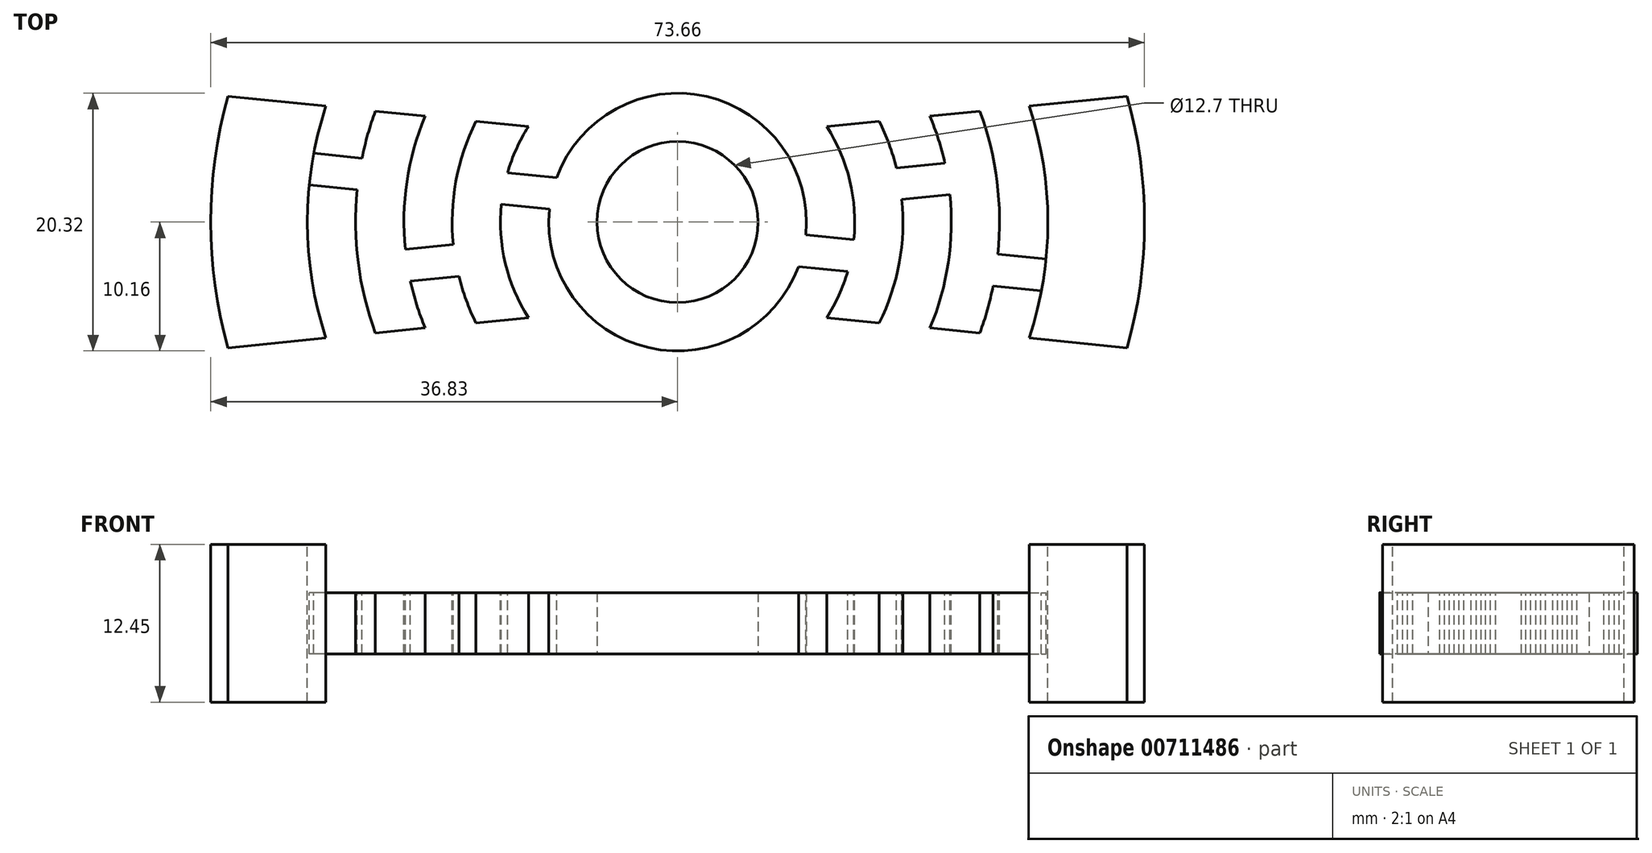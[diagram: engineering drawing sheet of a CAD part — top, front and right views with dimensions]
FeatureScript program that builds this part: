
annotation { "Feature Type Name" : "Feature", "Feature Type Description" : "" }
export const myFeature = defineFeature(function(context is Context, id is Id, definition is map)
    precondition{}
    {
        {
            var Q0;
            Q0=qCreatedBy(makeId("Top.planeOp"),FACE);
            var sketch = newSketch(context, id + "F0", { "sketchPlane" : qUnion([Q0])});
            skCircle(sketch, "E0", {"center": v(0, 0) * mm, "radius": 6.35 * mm});
            skCircle(sketch, "E1", {"center": v(0, 0) * mm, "radius": 10.16 * mm});
            skLineSegment(sketch, "E2", {"start": v(0, 6.35) * mm, "end": v(-37.9, 10.16) * mm});
            skLineSegment(sketch, "E3", {"start": v(0, -6.35) * mm, "end": v(-37.9, -10.16) * mm});
            skLineSegment(sketch, "E4", {"start": v(0, 6.35) * mm, "end": v(37.9, 10.16) * mm});
            skLineSegment(sketch, "E5", {"start": v(0, -6.35) * mm, "end": v(37.9, -10.16) * mm});
            skLineSegment(sketch, "E6", {"start": v(0, 0) * mm, "end": v(40.64, 0) * mm});
            skLineSegment(sketch, "E7", {"start": v(0, 0) * mm, "end": v(-40.64, 0) * mm});
            skCircle(sketch, "E8", {"center": v(0, 0) * mm, "radius": 39.25 * mm});
            skSolve(sketch);
        }
        {
            var Q0;
            {var subQ0=sQuery(id+"F0.wireOp",EDGE,"E4");var subQ1=sQuery(id+"F0.wireOp",EDGE,"E1");var subQ2=makeQuery(id+"F0.imprint","INTERSECT",VERTEX,{"derivedFrom":[subQ1,subQ0]});Q0=makeQuery(id+"F0.imprint","IMPRINT",FACE,{"disambiguationData":[TD([[makeQuery(id+"F0.imprint","IMPRINT",EDGE,{"disambiguationData":[TD([[subQ2,1.0]])],"derivedFrom":subQ1}),-1.0]])]});}
            var Q1;
            {var subQ0=sQuery(id+"F0.wireOp",EDGE,"E2");var subQ1=sQuery(id+"F0.wireOp",EDGE,"E1");var subQ2=makeQuery(id+"F0.imprint","INTERSECT",VERTEX,{"derivedFrom":[subQ1,subQ0]});Q1=makeQuery(id+"F0.imprint","IMPRINT",FACE,{"disambiguationData":[TD([[makeQuery(id+"F0.imprint","IMPRINT",EDGE,{"disambiguationData":[TD([[subQ2,-1.0]])],"derivedFrom":subQ1}),-1.0]])]});}
            var Q2;
            {var subQ0=sQuery(id+"F0.wireOp",EDGE,"E7");var subQ1=sQuery(id+"F0.wireOp",EDGE,"E1");var subQ2=makeQuery(id+"F0.imprint","INTERSECT",VERTEX,{"derivedFrom":[subQ1,subQ0]});Q2=makeQuery(id+"F0.imprint","IMPRINT",FACE,{"disambiguationData":[TD([[makeQuery(id+"F0.imprint","IMPRINT",EDGE,{"disambiguationData":[TD([[subQ2,-1.0]])],"derivedFrom":subQ1}),-1.0]])]});}
            var Q3;
            {var subQ0=sQuery(id+"F0.wireOp",EDGE,"E6");var subQ1=sQuery(id+"F0.wireOp",EDGE,"E1");var subQ2=makeQuery(id+"F0.imprint","INTERSECT",VERTEX,{"derivedFrom":[subQ1,subQ0]});Q3=makeQuery(id+"F0.imprint","IMPRINT",FACE,{"disambiguationData":[TD([[makeQuery(id+"F0.imprint","IMPRINT",EDGE,{"disambiguationData":[TD([[subQ2,1.0]])],"derivedFrom":subQ1}),-1.0]])]});}
            var Q4;
            {var subQ0=sQuery(id+"F0.wireOp",EDGE,"E2");var subQ5=sQuery(id+"F0.wireOp",EDGE,"E1");var subQ6=makeQuery(id+"F0.imprint","INTERSECT",VERTEX,{"derivedFrom":[subQ5,subQ0]});Q4=makeQuery(id+"F0.imprint","IMPRINT",FACE,{"disambiguationData":[TD([[makeQuery(id+"F0.imprint","IMPRINT",EDGE,{"disambiguationData":[TD([[subQ6,-1.0]])],"derivedFrom":subQ5}),1.0]])]});}
            var Q5;
            {var subQ3=sQuery(id+"F0.wireOp",EDGE,"E7");var subQ5=sQuery(id+"F0.wireOp",EDGE,"E1");var subQ6=makeQuery(id+"F0.imprint","INTERSECT",VERTEX,{"derivedFrom":[subQ5,subQ3]});Q5=makeQuery(id+"F0.imprint","IMPRINT",FACE,{"disambiguationData":[TD([[makeQuery(id+"F0.imprint","IMPRINT",EDGE,{"disambiguationData":[TD([[subQ6,-1.0]])],"derivedFrom":subQ5}),1.0]])]});}
            var Q6;
            {var subQ3=sQuery(id+"F0.wireOp",EDGE,"E6");var subQ5=sQuery(id+"F0.wireOp",EDGE,"E1");var subQ6=makeQuery(id+"F0.imprint","INTERSECT",VERTEX,{"derivedFrom":[subQ5,subQ3]});Q6=makeQuery(id+"F0.imprint","IMPRINT",FACE,{"disambiguationData":[TD([[makeQuery(id+"F0.imprint","IMPRINT",EDGE,{"disambiguationData":[TD([[subQ6,1.0]])],"derivedFrom":subQ5}),1.0]])]});}
            var Q7;
            {var subQ0=sQuery(id+"F0.wireOp",EDGE,"E4");var subQ5=sQuery(id+"F0.wireOp",EDGE,"E1");var subQ6=makeQuery(id+"F0.imprint","INTERSECT",VERTEX,{"derivedFrom":[subQ5,subQ0]});Q7=makeQuery(id+"F0.imprint","IMPRINT",FACE,{"disambiguationData":[TD([[makeQuery(id+"F0.imprint","IMPRINT",EDGE,{"disambiguationData":[TD([[subQ6,1.0]])],"derivedFrom":subQ5}),1.0]])]});}
            var Q8;
            {var subQ0=sQuery(id+"F0.wireOp",EDGE,"E4");var subQ1=sQuery(id+"F0.wireOp",EDGE,"E1");var subQ2=makeQuery(id+"F0.imprint","INTERSECT",VERTEX,{"derivedFrom":[subQ1,subQ0]});Q8=makeQuery(id+"F0.imprint","IMPRINT",FACE,{"disambiguationData":[TD([[makeQuery(id+"F0.imprint","IMPRINT",EDGE,{"disambiguationData":[TD([[subQ2,-1.0]])],"derivedFrom":subQ1}),1.0]])]});}
            var Q9;
            {var subQ0=sQuery(id+"F0.wireOp",EDGE,"E3");var subQ1=sQuery(id+"F0.wireOp",EDGE,"E1");var subQ2=makeQuery(id+"F0.imprint","INTERSECT",VERTEX,{"derivedFrom":[subQ1,subQ0]});Q9=makeQuery(id+"F0.imprint","IMPRINT",FACE,{"disambiguationData":[TD([[makeQuery(id+"F0.imprint","IMPRINT",EDGE,{"disambiguationData":[TD([[subQ2,-1.0]])],"derivedFrom":subQ1}),1.0]])]});}
            extrude(context, id + "F1", {"entities" : qUnion([Q0, Q1, Q2, Q3, Q4, Q5, Q6, Q7, Q8, Q9]), "depth" : 4.83 * mm, "offsetDistance" : 25.4 * mm});
        }
        {
            var Q0;
            Q0=makeQuery(id+"F1.opExtrude","CAP_FACE",FACE,{"disambiguationData":[OSD([sQuery(id+"F0.wireOp",EDGE,"E0"),sQuery(id+"F0.wireOp",EDGE,"E1"),sQuery(id+"F0.wireOp",EDGE,"E2"),sQuery(id+"F0.wireOp",EDGE,"E3"),sQuery(id+"F0.wireOp",EDGE,"E4"),sQuery(id+"F0.wireOp",EDGE,"E5"),sQuery(id+"F0.wireOp",EDGE,"liuHo2mv-Kwf8-5aol-AB9t-589r57ZSycez"),sQuery(id+"F0.wireOp",EDGE,"nakFOlJR-s7SA-ednX-MnhK-JYGa1BLhNWg9")])],"isStart":false});
            var sketch = newSketch(context, id + "F2", { "sketchPlane" : qUnion([Q0])});
            skCircle(sketch, "E9", {"center": v(0, 0) * mm, "radius": 6.35 * mm});
            skCircle(sketch, "E10", {"center": v(0, 0) * mm, "radius": 10.16 * mm});
            skCircle(sketch, "E11", {"center": v(0, 0) * mm, "radius": 39.25 * mm});
            skCircle(sketch, "E12", {"center": v(0, 0) * mm, "radius": 33.02 * mm});
            skCircle(sketch, "E13", {"center": v(0, 0) * mm, "radius": 25.4 * mm});
            skCircle(sketch, "E14", {"center": v(0, 0) * mm, "radius": 21.59 * mm});
            skCircle(sketch, "E15", {"center": v(0, 0) * mm, "radius": 29.21 * mm});
            skCircle(sketch, "E16", {"center": v(0, 0) * mm, "radius": 13.97 * mm});
            skCircle(sketch, "E17", {"center": v(0, 0) * mm, "radius": 17.78 * mm});
            skCircle(sketch, "E18", {"center": v(0, 0) * mm, "radius": 2.54 * mm});
            skLineSegment(sketch, "E19", {"start": v(0, -2.54) * mm, "end": v(-38.72, -6.43) * mm});
            skLineSegment(sketch, "E20", {"start": v(0, 2.54) * mm, "end": v(-38.72, 6.43) * mm});
            skLineSegment(sketch, "E21", {"start": v(0, -2.54) * mm, "end": v(38.72, -6.43) * mm});
            skLineSegment(sketch, "E22", {"start": v(0, 2.54) * mm, "end": v(38.72, 6.43) * mm});
            skLineSegment(sketch, "E23", {"start": v(0, 0) * mm, "end": v(-39.05, 3.92) * mm});
            skLineSegment(sketch, "E24", {"start": v(0, 0) * mm, "end": v(39.05, 3.92) * mm});
            skLineSegment(sketch, "E25", {"start": v(0, 0) * mm, "end": v(39.05, -3.92) * mm});
            skLineSegment(sketch, "E26", {"start": v(0, 0) * mm, "end": v(-39.05, -3.92) * mm});
            skCircle(sketch, "E27", {"center": v(0, 0) * mm, "radius": 36.83 * mm});
            skCircle(sketch, "E28", {"center": v(0.53, -0.92) * mm, "radius": 41.7 * mm});
            skSolve(sketch);
        }
        {
            var Q0;
            {var subQ0=sQuery(id+"F2.wireOp",EDGE,"E20");var subQ1=sQuery(id+"F2.wireOp",EDGE,"E14");var subQ2=makeQuery(id+"F2.imprint","INTERSECT",VERTEX,{"derivedFrom":[subQ1,subQ0]});Q0=makeQuery(id+"F2.imprint","IMPRINT",FACE,{"disambiguationData":[TD([[makeQuery(id+"F2.imprint","IMPRINT",EDGE,{"disambiguationData":[TD([[subQ2,1.0]])],"derivedFrom":subQ1}),1.0]])]});}
            var Q1;
            {var subQ0=sQuery(id+"F2.wireOp",EDGE,"E20");var subQ1=sQuery(id+"F2.wireOp",EDGE,"E14");var subQ2=makeQuery(id+"F2.imprint","INTERSECT",VERTEX,{"derivedFrom":[subQ1,subQ0]});Q1=makeQuery(id+"F2.imprint","IMPRINT",FACE,{"disambiguationData":[TD([[makeQuery(id+"F2.imprint","IMPRINT",EDGE,{"disambiguationData":[TD([[subQ2,-1.0]])],"derivedFrom":subQ1}),1.0]])]});}
            var Q2;
            {var subQ0=sQuery(id+"F2.wireOp",EDGE,"E21");var subQ1=sQuery(id+"F2.wireOp",EDGE,"E14");var subQ2=makeQuery(id+"F2.imprint","INTERSECT",VERTEX,{"derivedFrom":[subQ1,subQ0]});Q2=makeQuery(id+"F2.imprint","IMPRINT",FACE,{"disambiguationData":[TD([[makeQuery(id+"F2.imprint","IMPRINT",EDGE,{"disambiguationData":[TD([[subQ2,1.0]])],"derivedFrom":subQ1}),1.0]])]});}
            var Q3;
            {var subQ0=sQuery(id+"F2.wireOp",EDGE,"E19");var subQ1=sQuery(id+"F2.wireOp",EDGE,"E14");var subQ2=makeQuery(id+"F2.imprint","INTERSECT",VERTEX,{"derivedFrom":[subQ1,subQ0]});Q3=makeQuery(id+"F2.imprint","IMPRINT",FACE,{"disambiguationData":[TD([[makeQuery(id+"F2.imprint","IMPRINT",EDGE,{"disambiguationData":[TD([[subQ2,-1.0]])],"derivedFrom":subQ1}),1.0]])]});}
            var Q4;
            {var subQ0=sQuery(id+"F2.wireOp",EDGE,"E19");var subQ1=sQuery(id+"F2.wireOp",EDGE,"E13");var subQ2=makeQuery(id+"F2.imprint","INTERSECT",VERTEX,{"derivedFrom":[subQ1,subQ0]});Q4=makeQuery(id+"F2.imprint","IMPRINT",FACE,{"disambiguationData":[TD([[makeQuery(id+"F2.imprint","IMPRINT",EDGE,{"disambiguationData":[TD([[subQ2,-1.0]])],"derivedFrom":subQ1}),-1.0]])]});}
            var Q5;
            {var subQ0=sQuery(id+"F2.wireOp",EDGE,"E23");var subQ1=sQuery(id+"F2.wireOp",EDGE,"E13");var subQ2=makeQuery(id+"F2.imprint","INTERSECT",VERTEX,{"derivedFrom":[subQ1,subQ0]});Q5=makeQuery(id+"F2.imprint","IMPRINT",FACE,{"disambiguationData":[TD([[makeQuery(id+"F2.imprint","IMPRINT",EDGE,{"disambiguationData":[TD([[subQ2,-1.0]])],"derivedFrom":subQ1}),-1.0]])]});}
            var Q6;
            {var subQ0=sQuery(id+"F2.wireOp",EDGE,"E20");var subQ1=sQuery(id+"F2.wireOp",EDGE,"E13");var subQ2=makeQuery(id+"F2.imprint","INTERSECT",VERTEX,{"derivedFrom":[subQ1,subQ0]});Q6=makeQuery(id+"F2.imprint","IMPRINT",FACE,{"disambiguationData":[TD([[makeQuery(id+"F2.imprint","IMPRINT",EDGE,{"disambiguationData":[TD([[subQ2,1.0]])],"derivedFrom":subQ1}),-1.0]])]});}
            var Q7;
            {var subQ0=sQuery(id+"F2.wireOp",EDGE,"E24");var subQ1=sQuery(id+"F2.wireOp",EDGE,"E14");var subQ2=makeQuery(id+"F2.imprint","INTERSECT",VERTEX,{"derivedFrom":[subQ1,subQ0]});Q7=makeQuery(id+"F2.imprint","IMPRINT",FACE,{"disambiguationData":[TD([[makeQuery(id+"F2.imprint","IMPRINT",EDGE,{"disambiguationData":[TD([[subQ2,1.0]])],"derivedFrom":subQ1}),1.0]])]});}
            var Q8;
            {var subQ0=sQuery(id+"F2.wireOp",EDGE,"E21");var subQ1=sQuery(id+"F2.wireOp",EDGE,"E14");var subQ2=makeQuery(id+"F2.imprint","INTERSECT",VERTEX,{"derivedFrom":[subQ1,subQ0]});Q8=makeQuery(id+"F2.imprint","IMPRINT",FACE,{"disambiguationData":[TD([[makeQuery(id+"F2.imprint","IMPRINT",EDGE,{"disambiguationData":[TD([[subQ2,-1.0]])],"derivedFrom":subQ1}),1.0]])]});}
            var Q9;
            {var subQ0=sQuery(id+"F2.wireOp",EDGE,"E22");var subQ1=sQuery(id+"F2.wireOp",EDGE,"E14");var subQ2=makeQuery(id+"F2.imprint","INTERSECT",VERTEX,{"derivedFrom":[subQ1,subQ0]});Q9=makeQuery(id+"F2.imprint","IMPRINT",FACE,{"disambiguationData":[TD([[makeQuery(id+"F2.imprint","IMPRINT",EDGE,{"disambiguationData":[TD([[subQ2,-1.0]])],"derivedFrom":subQ1}),1.0]])]});}
            var Q10;
            {var subQ0=sQuery(id+"F2.wireOp",EDGE,"E22");var subQ1=sQuery(id+"F2.wireOp",EDGE,"E13");var subQ2=makeQuery(id+"F2.imprint","INTERSECT",VERTEX,{"derivedFrom":[subQ1,subQ0]});Q10=makeQuery(id+"F2.imprint","IMPRINT",FACE,{"disambiguationData":[TD([[makeQuery(id+"F2.imprint","IMPRINT",EDGE,{"disambiguationData":[TD([[subQ2,-1.0]])],"derivedFrom":subQ1}),-1.0]])]});}
            var Q11;
            {var subQ0=sQuery(id+"F2.wireOp",EDGE,"E22");var subQ1=sQuery(id+"F2.wireOp",EDGE,"E13");var subQ2=makeQuery(id+"F2.imprint","INTERSECT",VERTEX,{"derivedFrom":[subQ1,subQ0]});Q11=makeQuery(id+"F2.imprint","IMPRINT",FACE,{"disambiguationData":[TD([[makeQuery(id+"F2.imprint","IMPRINT",EDGE,{"disambiguationData":[TD([[subQ2,1.0]])],"derivedFrom":subQ1}),-1.0]])]});}
            var Q12;
            {var subQ0=sQuery(id+"F2.wireOp",EDGE,"E24");var subQ1=sQuery(id+"F2.wireOp",EDGE,"E13");var subQ2=makeQuery(id+"F2.imprint","INTERSECT",VERTEX,{"derivedFrom":[subQ1,subQ0]});Q12=makeQuery(id+"F2.imprint","IMPRINT",FACE,{"disambiguationData":[TD([[makeQuery(id+"F2.imprint","IMPRINT",EDGE,{"disambiguationData":[TD([[subQ2,1.0]])],"derivedFrom":subQ1}),-1.0]])]});}
            var Q13;
            {var subQ0=sQuery(id+"F2.wireOp",EDGE,"E21");var subQ1=sQuery(id+"F2.wireOp",EDGE,"E13");var subQ2=makeQuery(id+"F2.imprint","INTERSECT",VERTEX,{"derivedFrom":[subQ1,subQ0]});Q13=makeQuery(id+"F2.imprint","IMPRINT",FACE,{"disambiguationData":[TD([[makeQuery(id+"F2.imprint","IMPRINT",EDGE,{"disambiguationData":[TD([[subQ2,1.0]])],"derivedFrom":subQ1}),-1.0]])]});}
            var Q14;
            {var subQ0=sQuery(id+"F2.wireOp",EDGE,"E23");var subQ1=sQuery(id+"F2.wireOp",EDGE,"E14");var subQ2=makeQuery(id+"F2.imprint","INTERSECT",VERTEX,{"derivedFrom":[subQ1,subQ0]});Q14=makeQuery(id+"F2.imprint","IMPRINT",FACE,{"disambiguationData":[TD([[makeQuery(id+"F2.imprint","IMPRINT",EDGE,{"disambiguationData":[TD([[subQ2,-1.0]])],"derivedFrom":subQ1}),1.0]])]});}
            var Q15;
            {var subQ0=sQuery(id+"F2.wireOp",EDGE,"E26");var subQ1=sQuery(id+"F2.wireOp",EDGE,"E13");var subQ2=makeQuery(id+"F2.imprint","INTERSECT",VERTEX,{"derivedFrom":[subQ1,subQ0]});Q15=makeQuery(id+"F2.imprint","IMPRINT",FACE,{"disambiguationData":[TD([[makeQuery(id+"F2.imprint","IMPRINT",EDGE,{"disambiguationData":[TD([[subQ2,-1.0]])],"derivedFrom":subQ1}),-1.0]])]});}
            var Q16;
            {var subQ0=sQuery(id+"F2.wireOp",EDGE,"E19");var subQ1=sQuery(id+"F2.wireOp",EDGE,"E11");var subQ2=makeQuery(id+"F2.imprint","INTERSECT",VERTEX,{"derivedFrom":[subQ1,subQ0]});Q16=makeQuery(id+"F2.imprint","IMPRINT",FACE,{"disambiguationData":[TD([[makeQuery(id+"F2.imprint","IMPRINT",EDGE,{"disambiguationData":[TD([[subQ2,1.0]])],"derivedFrom":subQ1}),1.0]])]});}
            var Q17;
            {var subQ0=sQuery(id+"F2.wireOp",EDGE,"E11");var subQ1=makeQuery(id+"F1.opExtrude","CAP_EDGE",EDGE,{"disambiguationData":[OSD([sQuery(id+"F0.wireOp",EDGE,"E3")])],"isStart":false});var subQ2=makeQuery(id+"F2.imprint","INTERSECT",VERTEX,{"derivedFrom":[subQ1,subQ0]});Q17=makeQuery(id+"F2.imprint","IMPRINT",FACE,{"disambiguationData":[TD([[makeQuery(id+"F2.imprint","IMPRINT",EDGE,{"disambiguationData":[TD([[subQ2,1.0]])],"derivedFrom":subQ0}),1.0]])]});}
            var Q18;
            {var subQ0=sQuery(id+"F2.wireOp",EDGE,"E23");var subQ1=sQuery(id+"F2.wireOp",EDGE,"E11");var subQ2=makeQuery(id+"F2.imprint","INTERSECT",VERTEX,{"derivedFrom":[subQ1,subQ0]});Q18=makeQuery(id+"F2.imprint","IMPRINT",FACE,{"disambiguationData":[TD([[makeQuery(id+"F2.imprint","IMPRINT",EDGE,{"disambiguationData":[TD([[subQ2,-1.0]])],"derivedFrom":subQ1}),1.0]])]});}
            var Q19;
            {var subQ0=sQuery(id+"F2.wireOp",EDGE,"E20");var subQ1=sQuery(id+"F2.wireOp",EDGE,"E11");var subQ2=makeQuery(id+"F2.imprint","INTERSECT",VERTEX,{"derivedFrom":[subQ1,subQ0]});Q19=makeQuery(id+"F2.imprint","IMPRINT",FACE,{"disambiguationData":[TD([[makeQuery(id+"F2.imprint","IMPRINT",EDGE,{"disambiguationData":[TD([[subQ2,-1.0]])],"derivedFrom":subQ1}),1.0]])]});}
            var Q20;
            {var subQ0=sQuery(id+"F2.wireOp",EDGE,"E11");var subQ1=makeQuery(id+"F1.opExtrude","CAP_EDGE",EDGE,{"disambiguationData":[OSD([sQuery(id+"F0.wireOp",EDGE,"E2")])],"isStart":false});var subQ2=makeQuery(id+"F2.imprint","INTERSECT",VERTEX,{"derivedFrom":[subQ1,subQ0]});Q20=makeQuery(id+"F2.imprint","IMPRINT",FACE,{"disambiguationData":[TD([[makeQuery(id+"F2.imprint","IMPRINT",EDGE,{"disambiguationData":[TD([[subQ2,-1.0]])],"derivedFrom":subQ0}),1.0]])]});}
            var Q21;
            {var subQ0=sQuery(id+"F2.wireOp",EDGE,"E11");var subQ1=makeQuery(id+"F1.opExtrude","CAP_EDGE",EDGE,{"disambiguationData":[OSD([sQuery(id+"F0.wireOp",EDGE,"E4")])],"isStart":false});var subQ2=makeQuery(id+"F2.imprint","INTERSECT",VERTEX,{"derivedFrom":[subQ1,subQ0]});Q21=makeQuery(id+"F2.imprint","IMPRINT",FACE,{"disambiguationData":[TD([[makeQuery(id+"F2.imprint","IMPRINT",EDGE,{"disambiguationData":[TD([[subQ2,1.0]])],"derivedFrom":subQ0}),1.0]])]});}
            var Q22;
            {var subQ0=sQuery(id+"F2.wireOp",EDGE,"E22");var subQ1=sQuery(id+"F2.wireOp",EDGE,"E11");var subQ2=makeQuery(id+"F2.imprint","INTERSECT",VERTEX,{"derivedFrom":[subQ1,subQ0]});Q22=makeQuery(id+"F2.imprint","IMPRINT",FACE,{"disambiguationData":[TD([[makeQuery(id+"F2.imprint","IMPRINT",EDGE,{"disambiguationData":[TD([[subQ2,1.0]])],"derivedFrom":subQ1}),1.0]])]});}
            var Q23;
            {var subQ0=sQuery(id+"F2.wireOp",EDGE,"E24");var subQ1=sQuery(id+"F2.wireOp",EDGE,"E11");var subQ2=makeQuery(id+"F2.imprint","INTERSECT",VERTEX,{"derivedFrom":[subQ1,subQ0]});Q23=makeQuery(id+"F2.imprint","IMPRINT",FACE,{"disambiguationData":[TD([[makeQuery(id+"F2.imprint","IMPRINT",EDGE,{"disambiguationData":[TD([[subQ2,1.0]])],"derivedFrom":subQ1}),1.0]])]});}
            var Q24;
            {var subQ0=sQuery(id+"F2.wireOp",EDGE,"E21");var subQ1=sQuery(id+"F2.wireOp",EDGE,"E11");var subQ2=makeQuery(id+"F2.imprint","INTERSECT",VERTEX,{"derivedFrom":[subQ1,subQ0]});Q24=makeQuery(id+"F2.imprint","IMPRINT",FACE,{"disambiguationData":[TD([[makeQuery(id+"F2.imprint","IMPRINT",EDGE,{"disambiguationData":[TD([[subQ2,-1.0]])],"derivedFrom":subQ1}),1.0]])]});}
            var Q25;
            {var subQ0=sQuery(id+"F2.wireOp",EDGE,"E11");var subQ1=makeQuery(id+"F1.opExtrude","CAP_EDGE",EDGE,{"disambiguationData":[OSD([sQuery(id+"F0.wireOp",EDGE,"E5")])],"isStart":false});var subQ2=makeQuery(id+"F2.imprint","INTERSECT",VERTEX,{"derivedFrom":[subQ1,subQ0]});Q25=makeQuery(id+"F2.imprint","IMPRINT",FACE,{"disambiguationData":[TD([[makeQuery(id+"F2.imprint","IMPRINT",EDGE,{"disambiguationData":[TD([[subQ2,-1.0]])],"derivedFrom":subQ0}),1.0]])]});}
            var Q26;
            {var subQ0=sQuery(id+"F2.wireOp",EDGE,"E10");var subQ1=makeQuery(id+"F1.opExtrude","CAP_EDGE",EDGE,{"disambiguationData":[OSD([sQuery(id+"F0.wireOp",EDGE,"E5")])],"isStart":false});var subQ2=makeQuery(id+"F2.imprint","INTERSECT",VERTEX,{"derivedFrom":[subQ1,subQ0]});Q26=makeQuery(id+"F2.imprint","IMPRINT",FACE,{"disambiguationData":[TD([[makeQuery(id+"F2.imprint","IMPRINT",EDGE,{"disambiguationData":[TD([[subQ2,-1.0]])],"derivedFrom":subQ0}),-1.0]])]});}
            var Q27;
            {var subQ0=sQuery(id+"F2.wireOp",EDGE,"E24");var subQ1=sQuery(id+"F2.wireOp",EDGE,"E10");var subQ2=makeQuery(id+"F2.imprint","INTERSECT",VERTEX,{"derivedFrom":[subQ1,subQ0]});Q27=makeQuery(id+"F2.imprint","IMPRINT",FACE,{"disambiguationData":[TD([[makeQuery(id+"F2.imprint","IMPRINT",EDGE,{"disambiguationData":[TD([[subQ2,1.0]])],"derivedFrom":subQ1}),-1.0]])]});}
            var Q28;
            {var subQ0=sQuery(id+"F2.wireOp",EDGE,"E22");var subQ1=sQuery(id+"F2.wireOp",EDGE,"E10");var subQ2=makeQuery(id+"F2.imprint","INTERSECT",VERTEX,{"derivedFrom":[subQ1,subQ0]});Q28=makeQuery(id+"F2.imprint","IMPRINT",FACE,{"disambiguationData":[TD([[makeQuery(id+"F2.imprint","IMPRINT",EDGE,{"disambiguationData":[TD([[subQ2,1.0]])],"derivedFrom":subQ1}),-1.0]])]});}
            var Q29;
            {var subQ0=sQuery(id+"F2.wireOp",EDGE,"E10");var subQ1=makeQuery(id+"F1.opExtrude","CAP_EDGE",EDGE,{"disambiguationData":[OSD([sQuery(id+"F0.wireOp",EDGE,"E4")])],"isStart":false});var subQ2=makeQuery(id+"F2.imprint","INTERSECT",VERTEX,{"derivedFrom":[subQ1,subQ0]});Q29=makeQuery(id+"F2.imprint","IMPRINT",FACE,{"disambiguationData":[TD([[makeQuery(id+"F2.imprint","IMPRINT",EDGE,{"disambiguationData":[TD([[subQ2,1.0]])],"derivedFrom":subQ0}),-1.0]])]});}
            var Q30;
            {var subQ0=sQuery(id+"F2.wireOp",EDGE,"E10");var subQ1=makeQuery(id+"F1.opExtrude","CAP_EDGE",EDGE,{"disambiguationData":[OSD([sQuery(id+"F0.wireOp",EDGE,"E2")])],"isStart":false});var subQ2=makeQuery(id+"F2.imprint","INTERSECT",VERTEX,{"derivedFrom":[subQ1,subQ0]});Q30=makeQuery(id+"F2.imprint","IMPRINT",FACE,{"disambiguationData":[TD([[makeQuery(id+"F2.imprint","IMPRINT",EDGE,{"disambiguationData":[TD([[subQ2,-1.0]])],"derivedFrom":subQ0}),-1.0]])]});}
            var Q31;
            {var subQ0=sQuery(id+"F2.wireOp",EDGE,"E23");var subQ1=sQuery(id+"F2.wireOp",EDGE,"E10");var subQ2=makeQuery(id+"F2.imprint","INTERSECT",VERTEX,{"derivedFrom":[subQ1,subQ0]});Q31=makeQuery(id+"F2.imprint","IMPRINT",FACE,{"disambiguationData":[TD([[makeQuery(id+"F2.imprint","IMPRINT",EDGE,{"disambiguationData":[TD([[subQ2,-1.0]])],"derivedFrom":subQ1}),-1.0]])]});}
            var Q32;
            {var subQ0=sQuery(id+"F2.wireOp",EDGE,"E26");var subQ1=sQuery(id+"F2.wireOp",EDGE,"E10");var subQ2=makeQuery(id+"F2.imprint","INTERSECT",VERTEX,{"derivedFrom":[subQ1,subQ0]});Q32=makeQuery(id+"F2.imprint","IMPRINT",FACE,{"disambiguationData":[TD([[makeQuery(id+"F2.imprint","IMPRINT",EDGE,{"disambiguationData":[TD([[subQ2,-1.0]])],"derivedFrom":subQ1}),-1.0]])]});}
            var Q33;
            {var subQ0=sQuery(id+"F2.wireOp",EDGE,"E10");var subQ1=makeQuery(id+"F1.opExtrude","CAP_EDGE",EDGE,{"disambiguationData":[OSD([sQuery(id+"F0.wireOp",EDGE,"E3")])],"isStart":false});var subQ2=makeQuery(id+"F2.imprint","INTERSECT",VERTEX,{"derivedFrom":[subQ1,subQ0]});Q33=makeQuery(id+"F2.imprint","IMPRINT",FACE,{"disambiguationData":[TD([[makeQuery(id+"F2.imprint","IMPRINT",EDGE,{"disambiguationData":[TD([[subQ2,1.0]])],"derivedFrom":subQ0}),-1.0]])]});}
            extrude(context, id + "F3", {"entities" : qUnion([Q0, Q1, Q2, Q3, Q4, Q5, Q6, Q7, Q8, Q9, Q10, Q11, Q12, Q13, Q14, Q15, Q16, Q17, Q18, Q19, Q20, Q21, Q22, Q23, Q24, Q25, Q26, Q27, Q28, Q29, Q30, Q31, Q32, Q33]), "operationType" : NewBodyOperationType.REMOVE, "oppositeDirection" : true, "depth" : 25.4 * mm, "offsetDistance" : 25.4 * mm});
        }
        {
            var Q0;
            Q0=makeQuery(id+"F1.opExtrude","CAP_FACE",FACE,{"disambiguationData":[OSD([sQuery(id+"F0.wireOp",EDGE,"E0"),sQuery(id+"F0.wireOp",EDGE,"E1"),sQuery(id+"F0.wireOp",EDGE,"E2"),sQuery(id+"F0.wireOp",EDGE,"E3"),sQuery(id+"F0.wireOp",EDGE,"E4"),sQuery(id+"F0.wireOp",EDGE,"E5"),sQuery(id+"F0.wireOp",EDGE,"E8")])],"isStart":false});
            var sketch = newSketch(context, id + "F4", { "sketchPlane" : qUnion([Q0])});
            skPoint(sketch, "E29", {"position": v(-36.83, 0) * mm});
            skPoint(sketch, "E30", {"position": v(36.83, 0) * mm});
            skLineSegment(sketch, "E31", {"start": v(-35.47, 9.91) * mm, "end": v(-27.74, 9.14) * mm});
            skLineSegment(sketch, "E32", {"start": v(-27.74, -9.14) * mm, "end": v(-35.47, -9.91) * mm});
            skLineSegment(sketch, "E33", {"start": v(27.74, 9.14) * mm, "end": v(35.47, 9.91) * mm});
            skLineSegment(sketch, "E34", {"start": v(35.47, -9.91) * mm, "end": v(27.74, -9.14) * mm});
            skArc(sketch, "E35", {"start": v(35.47, -9.91) * mm, "mid": v(36.83, 0) * mm, "end": v(35.47, 9.91) * mm});
            skArc(sketch, "E36", {"start": v(-35.47, 9.91) * mm, "mid": v(-36.83, 0) * mm, "end": v(-35.47, -9.91) * mm});
            skArc(sketch, "E37", {"start": v(-27.74, 9.14) * mm, "mid": v(-29.21, 0) * mm, "end": v(-27.74, -9.14) * mm});
            skArc(sketch, "E38", {"start": v(27.74, -9.14) * mm, "mid": v(29.21, 0) * mm, "end": v(27.74, 9.14) * mm});
            skSolve(sketch);
        }
        {
            var Q0;
            Q0 = qSketchRegion(id + "F4", true);
            extrude(context, id + "F5", {"entities" : qUnion([Q0]), "operationType" : NewBodyOperationType.ADD, "depth" : 3.8 * mm, "offsetDistance" : 25.4 * mm, "hasSecondDirection" : true, "secondDirectionOppositeDirection" : true, "secondDirectionDepth" : 8.64 * mm});
        }
    });
